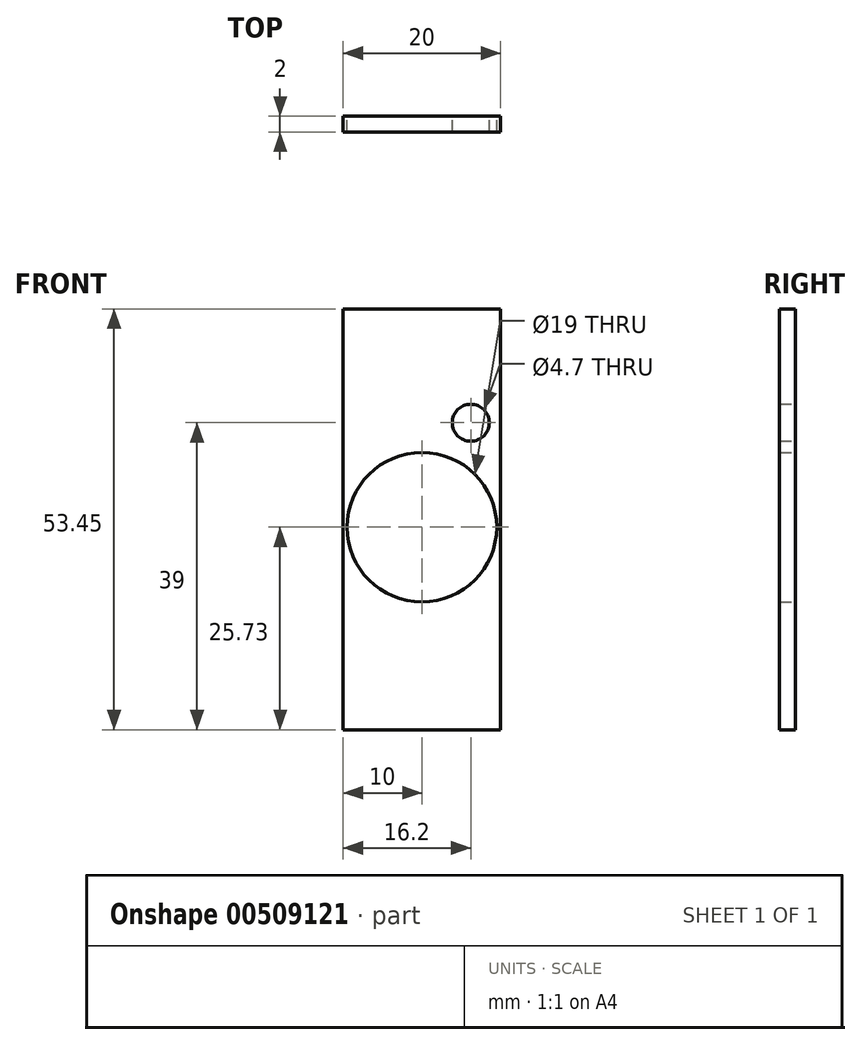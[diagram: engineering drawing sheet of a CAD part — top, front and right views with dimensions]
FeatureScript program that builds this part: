
annotation { "Feature Type Name" : "Feature", "Feature Type Description" : "" }
export const myFeature = defineFeature(function(context is Context, id is Id, definition is map)
    precondition{}
    {
        {
            var Q0;
            Q0=qCreatedBy(makeId("Front.planeOp"),FACE);
            var sketch = newSketch(context, id + "F0", { "sketchPlane" : qUnion([Q0])});
            skLineSegment(sketch, "E0.top", {"start": v(-10, -23.54) * mm, "end": v(10, -23.54) * mm});
            skLineSegment(sketch, "E0.left", {"start": v(-10, 29.9) * mm, "end": v(-10, -23.54) * mm});
            skLineSegment(sketch, "E0.right", {"start": v(10, 29.9) * mm, "end": v(10, -23.54) * mm});
            skPoint(sketch, "E0.middle", {"position": v(0, 0) * mm});
            skPoint(sketch, "E1.middle", {"position": v(0, 39.75) * mm});
            skCircle(sketch, "E2", {"center": v(6.2, 15.46) * mm, "radius": 2.35 * mm});
            skPoint(sketch, "E3", {"position": v(-10, 8.32) * mm});
            skPoint(sketch, "E4", {"position": v(-10, -13.68) * mm});
            skPoint(sketch, "E5", {"position": v(10, 8.35) * mm});
            skPoint(sketch, "E6", {"position": v(10, -13.65) * mm});
            skCircle(sketch, "E7", {"center": v(0, 2.19) * mm, "radius": 9.5 * mm});
            skLineSegment(sketch, "E8.top", {"start": v(-9.25, 29.9) * mm, "end": v(9.25, 29.9) * mm});
            skLineSegment(sketch, "E9", {"start": v(-9.25, 29.9) * mm, "end": v(-10, 29.9) * mm});
            skLineSegment(sketch, "E10", {"start": v(9.25, 29.9) * mm, "end": v(10, 29.9) * mm});
            skPoint(sketch, "E11.orphan", {"position": v(-10, 23.54) * mm});
            skPoint(sketch, "E12.orphan", {"position": v(10, 23.54) * mm});
            skLineSegment(sketch, "E13", {"start": v(6.2, 15.46) * mm, "end": v(-10, 15.46) * mm});
            skSolve(sketch);
        }
        {
            var Q0;
            {var subQ1=sQuery(id+"F0.wireOp",EDGE,"E0.top");Q0=makeQuery(id+"F0.imprint","IMPRINT",FACE,{"disambiguationData":[TD([[makeQuery(id+"F0.imprint","IMPRINT",EDGE,{"derivedFrom":subQ1}),1.0]])]});}
            extrude(context, id + "F1", {"entities" : qUnion([Q0]), "depth" : 2 * mm});
        }
    });
